# Revit family: KG273 Anti ligature grab bar 30in
name_source: partatom
category: Generic Models
revit_build: Autodesk Revit 2016 (Build: 20150701_1515(x64)
units: mm (PartAtom-declared; Revit-internal decimal feet)

## family parameters
Always vertical = Yes
Can host rebar = No
Cut with Voids When Loaded = No
Part Type = Normal
Room Calculation Point = No
Round Connector Dimension = Use Diameter
Shared = No
Work Plane-Based = No

## types (1)
- KG273 Anti ligature grab bar 30in
    Description = Grab bar is suitable for use in washrooms and shower areas and and can be installed both vertically and horizontally.  Specially designed open and closed end caps ensure ligature resistance and allow for easy cleaning and drainage.   Available in a variety of color options from the RAL color system.
    Finish = Steel - Blue
    Manufacturer = Kingsway Group Inc
    Model = KG273 Anti ligature grab bar 30"
    Telephone = 1-248-429-5520
    Type Comments = Available in LH (left hand handling) or RH (right hand handling). This needs to be specified when ordering.
    URL = https://www.kingswaygroupusa.com

## geometry (parser evidence)
native form markers: Sweep x2
no freeform markers — native parametric forms only
